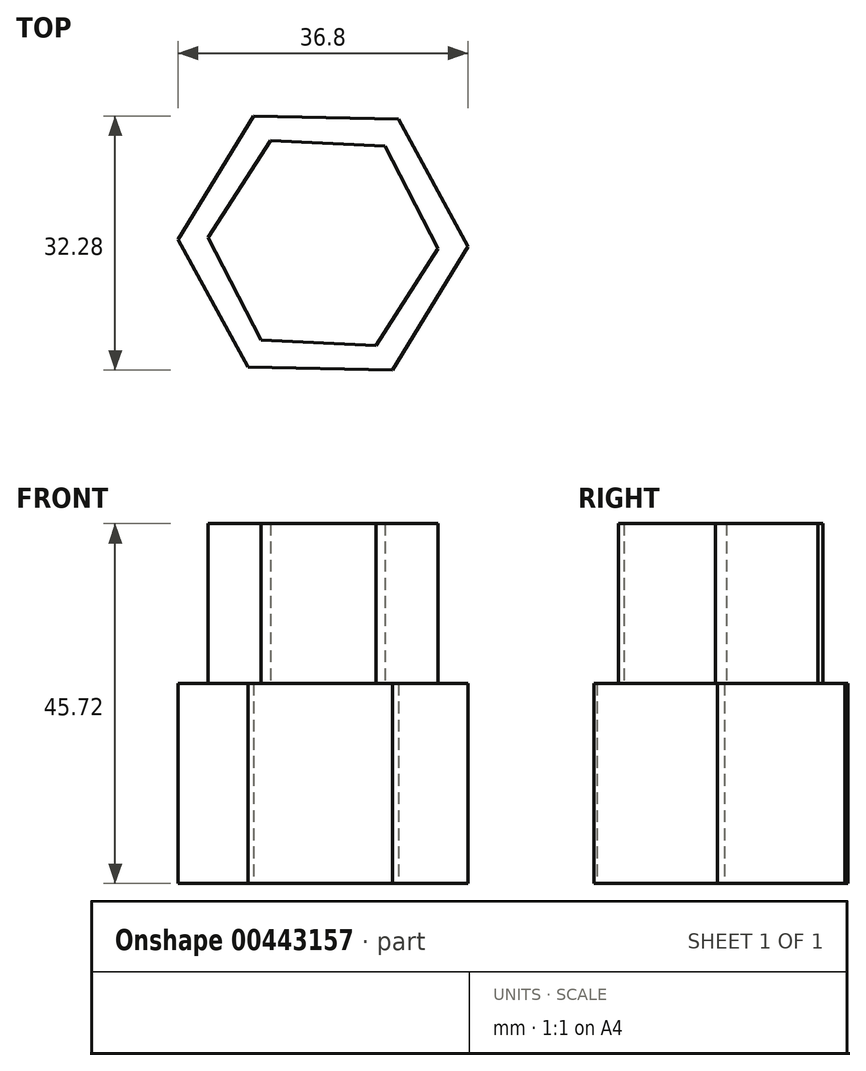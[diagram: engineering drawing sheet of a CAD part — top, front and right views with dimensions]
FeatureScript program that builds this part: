
annotation { "Feature Type Name" : "Feature", "Feature Type Description" : "" }
export const myFeature = defineFeature(function(context is Context, id is Id, definition is map)
    precondition{}
    {
        {
            var Q0;
            Q0=qCreatedBy(makeId("Top.planeOp"),FACE);
            var sketch = newSketch(context, id + "F0", { "sketchPlane" : qUnion([Q0])});
            skCircle(sketch, "E0.cCircle", {"center": v(0, 0) * mm, "radius": 15.94 * mm, "construction": true});
            skLineSegment(sketch, "E0.0", {"start": v(9.56, 15.73) * mm, "end": v(18.4, -0.42) * mm});
            skLineSegment(sketch, "E0.1", {"start": v(18.4, -0.42) * mm, "end": v(8.84, -16.14) * mm});
            skLineSegment(sketch, "E0.2", {"start": v(8.84, -16.14) * mm, "end": v(-9.56, -15.73) * mm});
            skLineSegment(sketch, "E0.3", {"start": v(-9.56, -15.73) * mm, "end": v(-18.4, 0.42) * mm});
            skLineSegment(sketch, "E0.4", {"start": v(-18.4, 0.42) * mm, "end": v(-8.84, 16.14) * mm});
            skLineSegment(sketch, "E0.5", {"start": v(-8.84, 16.14) * mm, "end": v(9.56, 15.73) * mm});
            skPoint(sketch, "E0.0.midPoint", {"position": v(13.98, 7.66) * mm});
            skSolve(sketch);
        }
        {
            var Q0;
            Q0 = qSketchRegion(id + "F0", true);
            extrude(context, id + "F1", {"entities" : qUnion([Q0]), "depth" : 25.4 * mm});
        }
        {
            var Q0;
            Q0=makeQuery(id+"F1.opExtrude","CAP_FACE",FACE,{"disambiguationData":[OSD([sQuery(id+"F0.wireOp",EDGE,"E0.0"),sQuery(id+"F0.wireOp",EDGE,"E0.1"),sQuery(id+"F0.wireOp",EDGE,"E0.2"),sQuery(id+"F0.wireOp",EDGE,"E0.3"),sQuery(id+"F0.wireOp",EDGE,"E0.4"),sQuery(id+"F0.wireOp",EDGE,"E0.5")])],"isStart":false});
            var sketch = newSketch(context, id + "F2", { "sketchPlane" : qUnion([Q0])});
            skCircle(sketch, "E1.cCircle", {"center": v(0, 0) * mm, "radius": 12.65 * mm, "construction": true});
            skLineSegment(sketch, "E1.0", {"start": v(-14.6, 0.7) * mm, "end": v(-6.7, 12.99) * mm});
            skLineSegment(sketch, "E1.1", {"start": v(-6.7, 12.99) * mm, "end": v(7.9, 12.3) * mm});
            skLineSegment(sketch, "E1.2", {"start": v(7.9, 12.3) * mm, "end": v(14.6, -0.7) * mm});
            skLineSegment(sketch, "E1.3", {"start": v(14.6, -0.7) * mm, "end": v(6.7, -12.99) * mm});
            skLineSegment(sketch, "E1.4", {"start": v(6.7, -12.99) * mm, "end": v(-7.9, -12.3) * mm});
            skLineSegment(sketch, "E1.5", {"start": v(-7.9, -12.3) * mm, "end": v(-14.6, 0.7) * mm});
            skPoint(sketch, "E1.0.midPoint", {"position": v(-10.65, 6.84) * mm});
            skSolve(sketch);
        }
        {
            var Q0;
            Q0 = qSketchRegion(id + "F2", true);
            extrude(context, id + "F3", {"entities" : qUnion([Q0]), "operationType" : NewBodyOperationType.ADD, "depth" : 20.32 * mm});
        }
    });
